# Revit family: 3-6054-xx Xani pendant
name_source: partatom
category: Luminarias
units: mm (PartAtom-declared; Revit-internal decimal feet)

## family parameters
Anfitrión = Techo
Compartido = No
Corte con vacíos al cargar = No
Cota de conector redondo = Diámetro de uso
Número OmniClass = 23.80.70.11
Origen de luz = Sí
Punto de cálculo de habitación = No
Siempre vertical = Sí
Tipo de pieza = Normal
Título OmniClass = Luminaries for Internal Lighting

## types (2) — shared parameters
Archivo de red fotométrica = 3-6054-15 Xanni 35 Pendant.ies
Cambio de temperatura de color de luz atenuada = <Ninguno>
Comentarios de vataje = 26.64 W at 120 V
Fabricante = Oxygen Lighting
Filtro de color = 16777215
Lámpara = LED
Main Diffuser = Matte White Acrylic
Modelo = 3-6054-xxx Xani (Pendant)
References = Ref. 3 = 120 V / Ref. 37 = 277 V
Voltage = 277 V
Voltage Input = 120 V or 277 V - 50/60 Hz
Ángulo de inclinación = 90.00°
zero-valued in all types: Elevación por defecto

## per-type parameters (varying)
| type | Metal Finish |
| 3-6054-15 / Black - Matte White Acrylic | 15 - Black |
| 3-6054-40 / Aged Brass - Matte White Acrylic | 40 - Aged Brass |

## geometry (parser evidence)
native form markers: Sweep x2
no freeform markers — native parametric forms only
